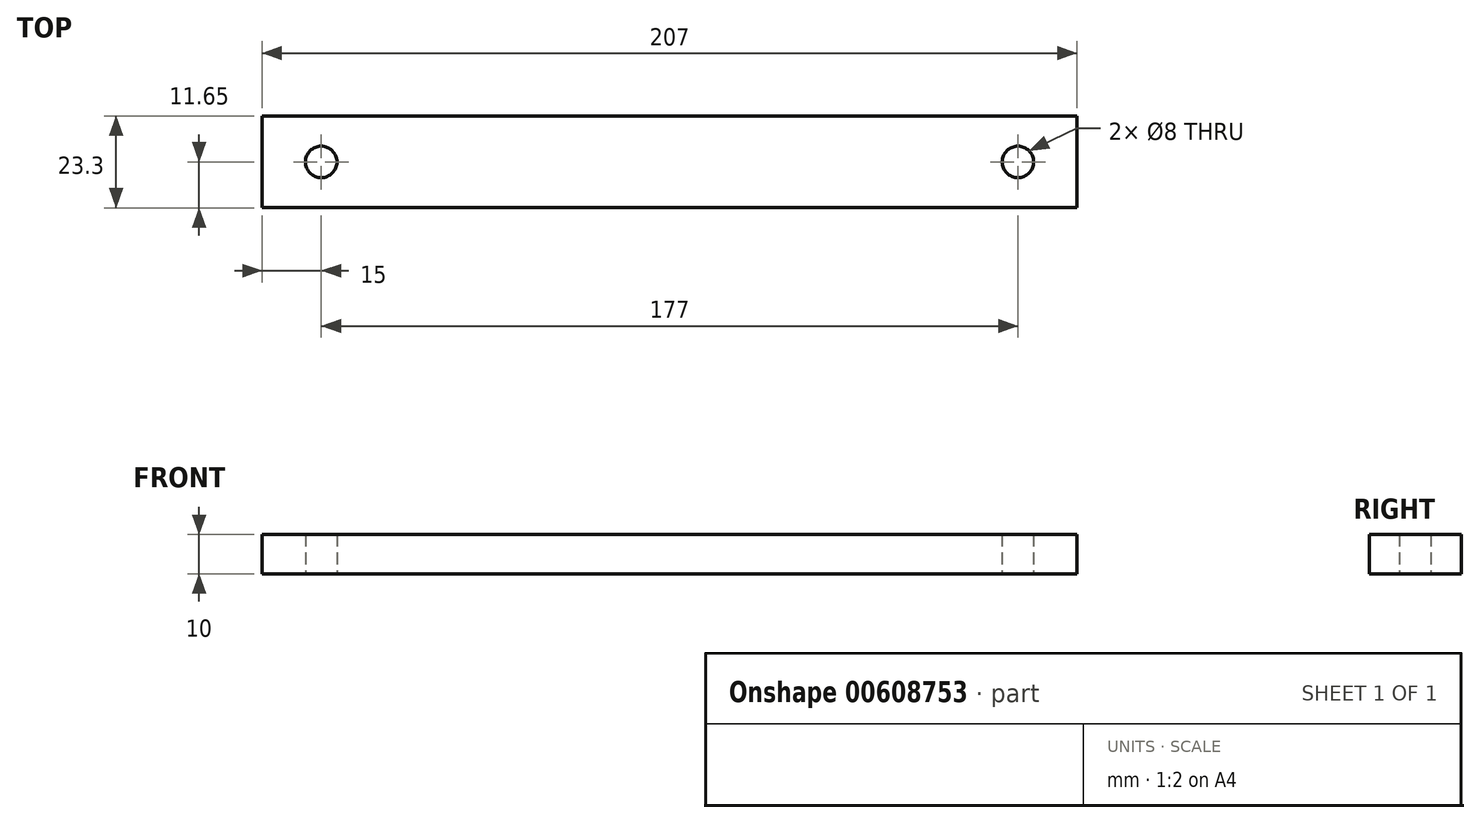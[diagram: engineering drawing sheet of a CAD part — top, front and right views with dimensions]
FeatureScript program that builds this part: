
annotation { "Feature Type Name" : "Feature", "Feature Type Description" : "" }
export const myFeature = defineFeature(function(context is Context, id is Id, definition is map)
    precondition{}
    {
        {
            var Q0;
            Q0=qCreatedBy(makeId("Top.planeOp"),FACE);
            var sketch = newSketch(context, id + "F0", { "sketchPlane" : qUnion([Q0])});
            skLineSegment(sketch, "E0.bottom", {"start": v(103.5, -11.65) * mm, "end": v(-103.5, -11.65) * mm});
            skLineSegment(sketch, "E0.top", {"start": v(103.5, 11.65) * mm, "end": v(-103.5, 11.65) * mm});
            skLineSegment(sketch, "E0.left", {"start": v(103.5, -11.65) * mm, "end": v(103.5, 11.65) * mm});
            skLineSegment(sketch, "E0.right", {"start": v(-103.5, -11.65) * mm, "end": v(-103.5, 11.65) * mm});
            skPoint(sketch, "E0.middle", {"position": v(0, 0) * mm});
            skCircle(sketch, "E1", {"center": v(88.5, 0) * mm, "radius": 4 * mm});
            skCircle(sketch, "E2", {"center": v(-88.5, 0) * mm, "radius": 4 * mm});
            skSolve(sketch);
        }
        {
            var Q0;
            Q0=makeQuery(id+"F0.imprint","IMPRINT",FACE,{"disambiguationData":[TD([[makeQuery(id+"F0.imprint","IMPRINT",EDGE,{"derivedFrom":sQuery(id+"F0.wireOp",EDGE,"E0.bottom")}),-1.0]])]});
            extrude(context, id + "F1", {"entities" : qUnion([Q0]), "depth" : 10 * mm, "offsetDistance" : 25 * mm});
        }
    });
